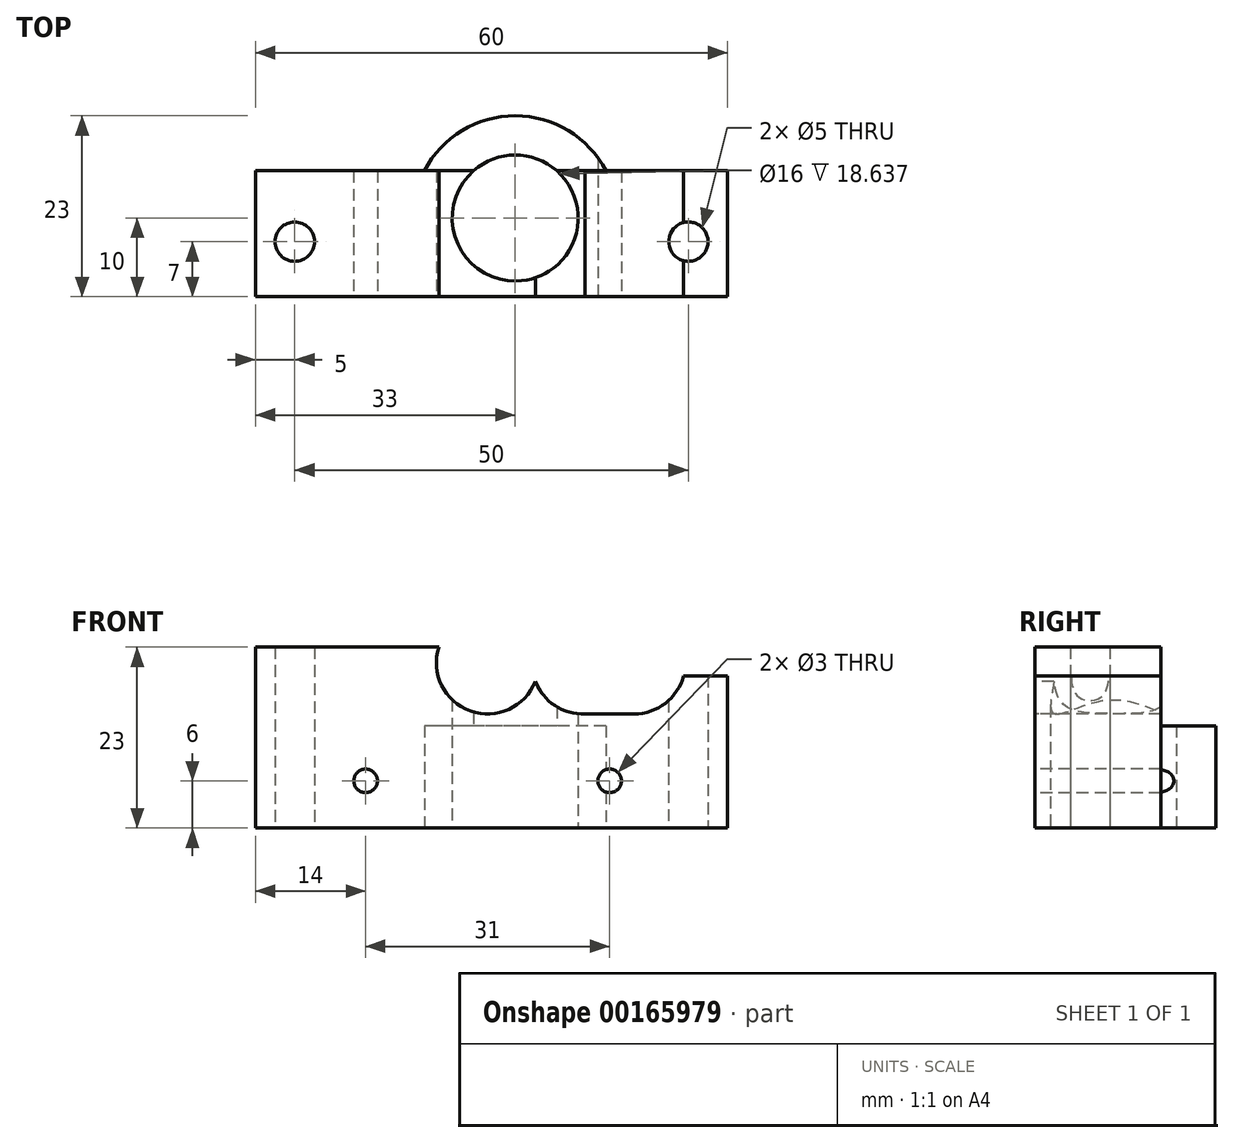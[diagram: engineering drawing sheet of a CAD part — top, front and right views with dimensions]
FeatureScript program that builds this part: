
annotation { "Feature Type Name" : "Feature", "Feature Type Description" : "" }
export const myFeature = defineFeature(function(context is Context, id is Id, definition is map)
    precondition{}
    {
        {
            var Q0;
            Q0=qCreatedBy(makeId("Top.planeOp"),FACE);
            var sketch = newSketch(context, id + "F0", { "sketchPlane" : qUnion([Q0])});
            skCircle(sketch, "E0", {"center": v(0, 0) * mm, "radius": 8 * mm});
            skLineSegment(sketch, "E1.bottom", {"start": v(-33, 6) * mm, "end": v(-11.53, 6) * mm});
            skLineSegment(sketch, "E1.top", {"start": v(-33, -10) * mm, "end": v(27, -10) * mm});
            skLineSegment(sketch, "E1.left", {"start": v(-33, 6) * mm, "end": v(-33, -10) * mm});
            skLineSegment(sketch, "E1.right", {"start": v(27, 6) * mm, "end": v(27, -10) * mm});
            skCircle(sketch, "E2", {"center": v(22, -3) * mm, "radius": 2.5 * mm});
            skCircle(sketch, "E3", {"center": v(-28, -3) * mm, "radius": 2.5 * mm});
            skArc(sketch, "E4", {"start": v(11.53, 6) * mm, "mid": v(0, 13) * mm, "end": v(-11.53, 6) * mm});
            skLineSegment(sketch, "E5.trimOffspring", {"start": v(11.53, 6) * mm, "end": v(27, 6) * mm});
            skSolve(sketch);
        }
        {
            var Q0;
            Q0 = qSketchRegion(id + "F0", true);
            extrude(context, id + "F1", {"entities" : qUnion([Q0]), "depth" : 23 * mm});
        }
        {
            var Q0;
            Q0=makeQuery(id+"F1.opExtrude","SWEPT_FACE",FACE,{"disambiguationData":[OSD([sQuery(id+"F0.wireOp",EDGE,"E1.top")])]});
            var sketch = newSketch(context, id + "F2", { "sketchPlane" : qUnion([Q0])});
            skCircle(sketch, "E6", {"center": v(-19, 6) * mm, "radius": 1.5 * mm});
            skCircle(sketch, "E7", {"center": v(12, 6) * mm, "radius": 1.5 * mm});
            skCircle(sketch, "E8", {"center": v(-3.5, 21) * mm, "radius": 6.5 * mm});
            skCircle(sketch, "E9", {"center": v(8.61, 21) * mm, "radius": 6.5 * mm});
            skCircle(sketch, "E10", {"center": v(15.11, 21) * mm, "radius": 6.5 * mm});
            skLineSegment(sketch, "E11", {"start": v(8.86, 14.5) * mm, "end": v(15.1, 14.5) * mm});
            skLineSegment(sketch, "E12", {"start": v(27, 19.36) * mm, "end": v(21.4, 19.36) * mm});
            skLineSegment(sketch, "E13", {"start": v(21.3, 23) * mm, "end": v(27, 23) * mm});
            skLineSegment(sketch, "E14", {"start": v(27, 23) * mm, "end": v(27, 19.36) * mm});
            skSolve(sketch);
        }
        {
            var Q0;
            Q0 = qSketchRegion(id + "F2", true);
            extrude(context, id + "F3", {"entities" : qUnion([Q0]), "operationType" : NewBodyOperationType.REMOVE, "endBound" : BoundingType.THROUGH_ALL, "oppositeDirection" : true, "depth" : 25 * mm});
        }
        {
            var Q0;
            Q0=makeQuery(id+"F1.opExtrude","SWEPT_FACE",FACE,{"disambiguationData":[OSD([sQuery(id+"F0.wireOp",EDGE,"E1.left")])]});
            var sketch = newSketch(context, id + "F4", { "sketchPlane" : qUnion([Q0])});
            skLineSegment(sketch, "E15.bottom", {"start": v(-6, 23) * mm, "end": v(-14, 23) * mm});
            skLineSegment(sketch, "E15.top", {"start": v(-6, 13) * mm, "end": v(-14, 13) * mm});
            skLineSegment(sketch, "E15.left", {"start": v(-6, 23) * mm, "end": v(-6, 13) * mm});
            skLineSegment(sketch, "E15.right", {"start": v(-14, 23) * mm, "end": v(-14, 13) * mm});
            skSolve(sketch);
        }
        {
            var Q0;
            Q0 = qSketchRegion(id + "F4", true);
            extrude(context, id + "F5", {"entities" : qUnion([Q0]), "operationType" : NewBodyOperationType.REMOVE, "endBound" : BoundingType.THROUGH_ALL, "oppositeDirection" : true, "depth" : 25 * mm});
        }
    });
